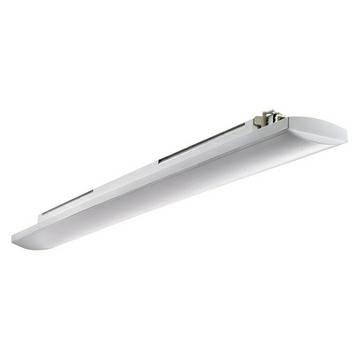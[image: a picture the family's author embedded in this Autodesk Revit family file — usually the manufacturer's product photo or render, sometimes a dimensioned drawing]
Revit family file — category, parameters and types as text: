
# Revit family: Lighting-Industrial-GEWISS-SMART[3]-WATERTIGHT-LED_OPAL_1200mm
name_source: partatom
category: Apparecchi per illuminazione
units: mm (PartAtom-declared; Revit-internal decimal feet)

## family parameters
Condiviso = No
Host = Superficie
Numero OmniClass = 23.80.70.11
Punto di calcolo locali = Sì
Quota connettore circolare = Usa diametro
Sorgente d'illuminazione = No
Taglio con vuoti quando caricato = No
Tipo di parte = Normale
Titolo OmniClass = Luminaries for Internal Lighting

## types (1)
- Lighting-Industrial-GEWISS-SMART[3]-WATERTIGHT-LED_OPAL_1200mm
    Application = Internal
    Carico apparente = 45 VA
    Catalogue = LIGHTING
    Catalogue Range = SMART [3]
    Colour temperature = 3000 K (CRI 80)
    Colour temperature: = 3000 K (CRI 80)
    Commenti sul wattaggio = 45W
    Descrizione = SMART3 1200 63LED OPALE DALI 30K
    Device with reduced surface temperature = Complying
    Driver type = Constant Current Driver Led
    EAN code = 8011564877061
    Efficiency class of integrated LEDs = A ÷ A++
    Electrocod = 2434
    Failure rate apparecchio (35.000h, Tq=35° C) = <2,5%
    Failure rate apparecchio (50.000h, Tq=25° C) = <2,5%
    Ganci = GEWISS  - ALLUMINIO
    Glow Wire Test = 850°C
    IDF = ad29ddb6-f95d-4c90-95e8-3fbb30e2f282
    IDT = 6d1ae202-d28e-42ab-a03c-f890c181dcac
    IP degree = IP66/IP69
    Immagine tipo = GWS3136P.jpg
    Insulation class = II
    LED Life Time (L90B50) = 50000H
    LED Life time (L70) = 80000H
    LED Life time (L80B50) = 100000H
    LED LifeTime (L80B20) = 85000H
    Lamp = LED
    Lampada = LED
    Length = 1200 mm
    Lumen output (lm) = 4500
    Lunghezza Lampada = 1200 mm
    Modello = GWS3236PD30K
    No. LED (#) = 63
    Nominal flux (lm) = 5500
    Operating temperature: = -30 +50 °C
    Produttore = GEWISS S.p.A.
    Prospetto di default = 1219 mm
    SEO = Luminaire
    Schermo. = Gewiss - Led Acceso
    Shield type = Opal
    Shock resistance = IK08
    Stampa 1_100 = Sì
    Stampa 1_200 = No
    Struttura = GEWISS - SMART 3 - GRIGIO
    System power = 40W
    Technical sheet = https://www.gewiss.com
    Type of light source = LED - Not replaceable
    Typology = DALI
    URL = https://www.gewiss.com
    Version file RFA = 20.11
    Voltage = 220/240 V - 50/60 Hz - Dali
    Warranty = 5 years
    Weight (kg): = 2
    Working temperature = -25 +50 °C
